# Revit family: QF_ELECTROLUXPROFESSIONAL_391204_E9PCEH2MF2
name_source: partatom
category: Specialty Equipment
revit_build: Autodesk Revit 2018 (Build: 20190510_1515(x64)
units: mm (PartAtom-declared; Revit-internal decimal feet)

## family parameters
Always vertical = Yes
Cut with Voids When Loaded = No
Part Type = Normal
Room Calculation Point = No
Round Connector Dimension = Use Diameter
Shared = No
Work Plane-Based = No

## types (1)
- QF_ELECTROLUXPROFESSIONAL_391204_E9PCEH2MF2
    Apparent Power = 20000 VA
    Cold Water Connection Height = 0 mm  [stored 0 ft]
    Cold Water Maximum Pressure = 0.00 psi
    Cold Water Minimum Pressure = 0.00 psi
    Cold Water Size = 1"
    Conn Conduit = Yes
    Depth = 930 mm  [stored 3.05118 ft]
    Description = ELECTRIC PASTA COOKER 2X40 LT WELLS-208V
    Direct Waste Size = 1"
    FL Amps = 56 A
    HP = 26.8 HP
    Height = 851 mm
    Indirect Waste Connection Height = 0 mm  [stored 0 ft]
    Indirect Waste Size = 1"
    Manufacturer = ELECTROLUX
    Max Overcurrent Protection = 0 A
    Min Ckt Ampacity = 0 A
    Model = 391204
    Phase = 3
    URL = www.electrolux.com/foodservice
    URL Cutsheet = www.electrolux.com/foodservice
    Volts = 208 V
    Watts = 20000 W
    Weight in Pounds = 253.5
    Width = 800 mm  [stored 2.62467 ft]

note: [stored X ft] marks values corroborated as IEEE doubles in the binary element streams (Revit-internal decimal feet)

## geometry (parser evidence)
native form markers: Blend x12, Sweep x2
no freeform markers — native parametric forms only
